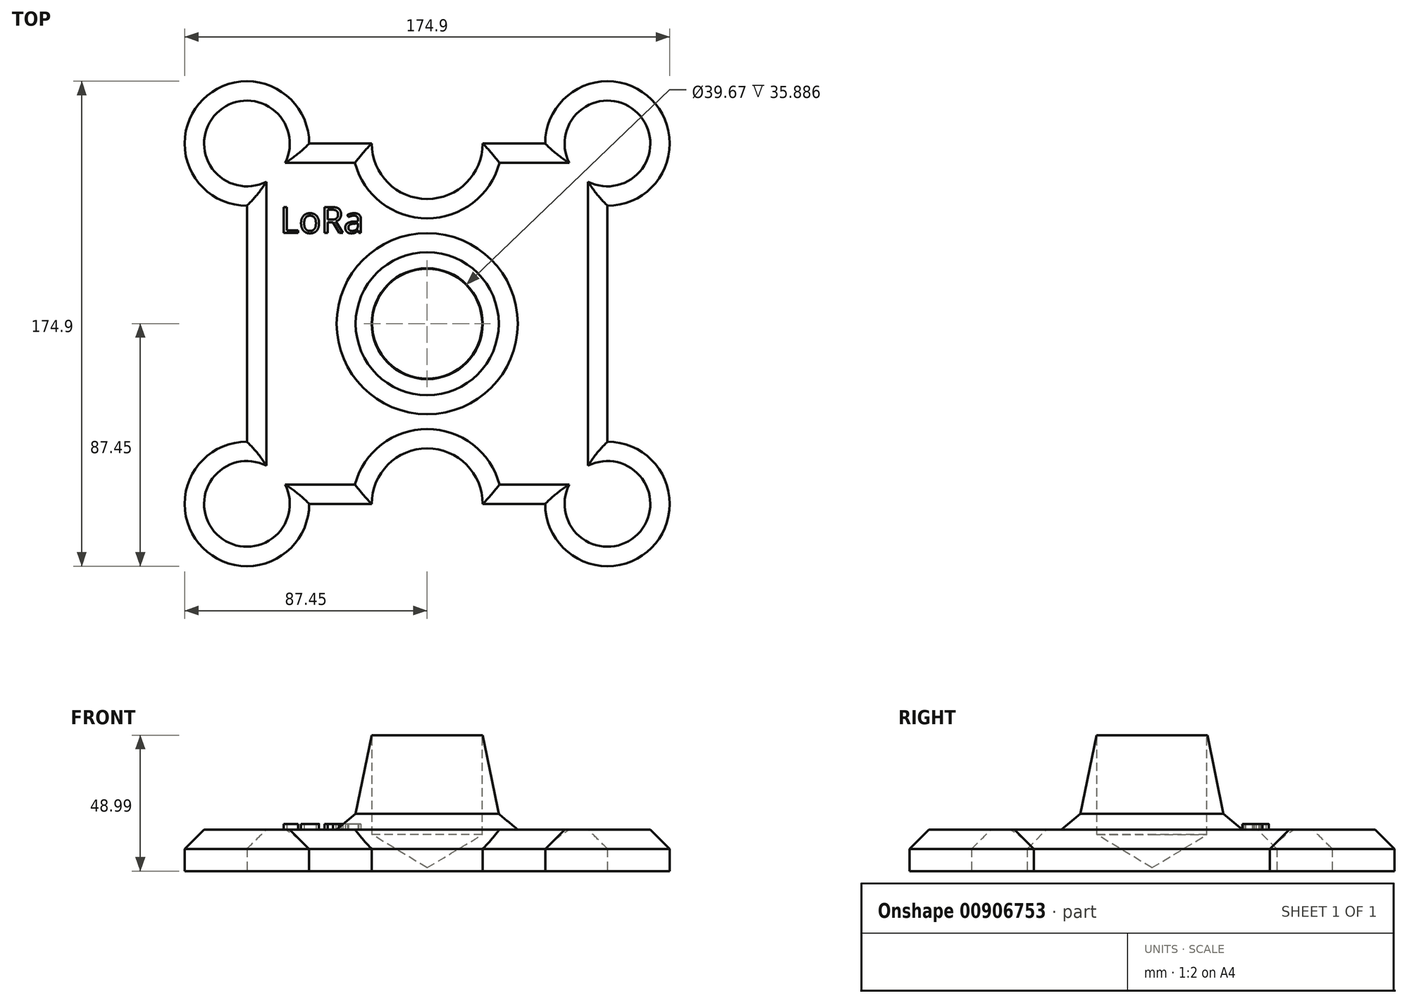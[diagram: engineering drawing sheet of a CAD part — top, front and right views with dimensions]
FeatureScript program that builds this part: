
annotation { "Feature Type Name" : "Feature", "Feature Type Description" : "" }
export const myFeature = defineFeature(function(context is Context, id is Id, definition is map)
    precondition{}
    {
        {
            var Q0;
            Q0=qCreatedBy(makeId("Top.planeOp"),FACE);
            var sketch = newSketch(context, id + "F0", { "sketchPlane" : qUnion([Q0])});
            skLineSegment(sketch, "E0.bottom", {"start": v(-42.55, 65) * mm, "end": v(-20, 65) * mm});
            skLineSegment(sketch, "E0.top", {"start": v(-42.55, -65) * mm, "end": v(-20, -65) * mm});
            skLineSegment(sketch, "E0.left", {"start": v(-65, 42.55) * mm, "end": v(-65, -42.55) * mm});
            skLineSegment(sketch, "E0.right", {"start": v(65, 42.55) * mm, "end": v(65, -42.55) * mm});
            skPoint(sketch, "E0.middle", {"position": v(0, 0) * mm});
            skArc(sketch, "E1", {"start": v(-42.55, 65) * mm, "mid": v(-80.87, 80.87) * mm, "end": v(-65, 42.55) * mm});
            skArc(sketch, "E2.1.0.0", {"start": v(-20, 65) * mm, "mid": v(0, 45) * mm, "end": v(20, 65) * mm});
            skArc(sketch, "E2.2.0.0", {"start": v(65, 42.55) * mm, "mid": v(80.87, 80.87) * mm, "end": v(42.55, 65) * mm});
            skLineSegment(sketch, "E2.direction1", {"start": v(-42.55, 65) * mm, "end": v(-20, 65) * mm, "construction": true});
            skArc(sketch, "E3.0.1.0", {"start": v(-65, -42.55) * mm, "mid": v(-80.87, -80.87) * mm, "end": v(-42.55, -65) * mm});
            skArc(sketch, "E3.1.1.0", {"start": v(20, -65) * mm, "mid": v(0, -45) * mm, "end": v(-20, -65) * mm});
            skArc(sketch, "E3.2.1.0", {"start": v(42.55, -65) * mm, "mid": v(80.87, -80.87) * mm, "end": v(65, -42.55) * mm});
            skLineSegment(sketch, "E3.direction2", {"start": v(-65, 42.55) * mm, "end": v(-65, -42.55) * mm, "construction": true});
            skLineSegment(sketch, "E4.trimOffspring", {"start": v(20, 65) * mm, "end": v(42.55, 65) * mm});
            skLineSegment(sketch, "E5.trimOffspring", {"start": v(20, -65) * mm, "end": v(42.55, -65) * mm});
            skSolve(sketch);
        }
        {
            var Q0;
            Q0=makeQuery(id+"F0.imprint","IMPRINT",FACE,{"disambiguationData":[TD([[makeQuery(id+"F0.imprint","IMPRINT",EDGE,{"derivedFrom":sQuery(id+"F0.wireOp",EDGE,"E0.bottom")}),-1.0]])]});
            extrude(context, id + "F1", {"entities" : qUnion([Q0]), "depth" : 15 * mm, "offsetDistance" : 25 * mm});
        }
        {
            var Q0;
            Q0=qCreatedBy(makeId("Front.planeOp"),FACE);
            var sketch = newSketch(context, id + "F2", { "sketchPlane" : qUnion([Q0])});
            skLineSegment(sketch, "E6", {"start": v(0, 0) * mm, "end": v(30, 0) * mm});
            skLineSegment(sketch, "E7", {"start": v(30, 0) * mm, "end": v(20, 48.99) * mm});
            skLineSegment(sketch, "E8", {"start": v(20, 48.99) * mm, "end": v(0, 48.99) * mm});
            skLineSegment(sketch, "E9", {"start": v(0, 48.99) * mm, "end": v(0, 0) * mm});
            skSolve(sketch);
        }
        {
            var Q0;
            Q0 = qSketchRegion(id + "F2", true);
            var Q1;
            Q1=sQuery(id+"F2.wireOp",EDGE,"E9");
            revolve(context, id + "F3", {"operationType" : NewBodyOperationType.ADD, "surfaceOperationType" : NewSurfaceOperationType.NEW, "entities" : qUnion([Q0]), "axis" : qUnion([Q1]), "revolveType" : RevolveType.FULL});
        }
        {
            var Q0;
            Q0=makeQuery(id+"F3.opRevolve","SWEPT_FACE",FACE,{"disambiguationData":[OSD([sQuery(id+"F2.wireOp",EDGE,"E8")])]});
            var sketch = newSketch(context, id + "F4", { "sketchPlane" : qUnion([Q0])});
            skCircle(sketch, "E10", {"center": v(0, 0) * mm, "radius": 29.1 * mm});
            skSolve(sketch);
        }
        {
            var Q0;
            Q0=sQuery(id+"F4.wireOp",VERTEX,"E10.center");
            var Q1;
            Q1=makeQuery(id+"F1.opExtrude","SWEPT_BODY",BODY,{"disambiguationData":[OSD([sQuery(id+"F0.wireOp",EDGE,"E0.bottom"),sQuery(id+"F0.wireOp",EDGE,"E0.top"),sQuery(id+"F0.wireOp",EDGE,"E0.left"),sQuery(id+"F0.wireOp",EDGE,"E0.right"),sQuery(id+"F0.wireOp",EDGE,"E1"),sQuery(id+"F0.wireOp",EDGE,"E2.1.0.0"),sQuery(id+"F0.wireOp",EDGE,"E2.2.0.0"),sQuery(id+"F0.wireOp",EDGE,"E3.0.1.0"),sQuery(id+"F0.wireOp",EDGE,"E3.1.1.0"),sQuery(id+"F0.wireOp",EDGE,"E3.2.1.0"),sQuery(id+"F0.wireOp",EDGE,"E4.trimOffspring"),sQuery(id+"F0.wireOp",EDGE,"E5.trimOffspring")])]});
            hole(context, id + "F5", {"style" : HoleStyle.SIMPLE, "endStyle" : HoleEndStyle.BLIND, "standardTappedOrClearance" : lookupTablePath({ "fit" : "Close (ASME)", "standard" : "ANSI", "size" : "1 1/2", "type" : "Clearance" }), "standardBlindInLast" : lookupTablePath({ "fit" : "Close", "standard" : "ANSI", "size" : "1 1/2", "type" : "Clearance" }), "holeDiameter" : 39.67 * mm, "majorDiameter" : 31.75 * mm, "holeDepth" : 35.9 * mm, "isTappedThrough" : true, "tappedDepth" : 12 * mm, "tapClearance" : 3, "locations" : qUnion([Q0]), "scope" : qUnion([Q1])});
        }
        {
            var Q0;
            Q0=makeQuery(id+"F1.opExtrude","CAP_FACE",FACE,{"disambiguationData":[OSD([sQuery(id+"F0.wireOp",EDGE,"E0.bottom"),sQuery(id+"F0.wireOp",EDGE,"E0.top"),sQuery(id+"F0.wireOp",EDGE,"E0.left"),sQuery(id+"F0.wireOp",EDGE,"E0.right"),sQuery(id+"F0.wireOp",EDGE,"E1"),sQuery(id+"F0.wireOp",EDGE,"E2.1.0.0"),sQuery(id+"F0.wireOp",EDGE,"E2.2.0.0"),sQuery(id+"F0.wireOp",EDGE,"E3.0.1.0"),sQuery(id+"F0.wireOp",EDGE,"E3.1.1.0"),sQuery(id+"F0.wireOp",EDGE,"E3.2.1.0"),sQuery(id+"F0.wireOp",EDGE,"E4.trimOffspring"),sQuery(id+"F0.wireOp",EDGE,"E5.trimOffspring")])],"isStart":false});
            chamfer(context, id + "F6", {"entities" : qUnion([Q0]), "width" : 7 * mm, "tangentPropagation" : true});
        }
        {
            var Q0;
            Q0=makeQuery(id+"F1.opExtrude","CAP_FACE",FACE,{"disambiguationData":[OSD([sQuery(id+"F0.wireOp",EDGE,"E0.bottom"),sQuery(id+"F0.wireOp",EDGE,"E0.top"),sQuery(id+"F0.wireOp",EDGE,"E0.left"),sQuery(id+"F0.wireOp",EDGE,"E0.right"),sQuery(id+"F0.wireOp",EDGE,"E1"),sQuery(id+"F0.wireOp",EDGE,"E2.1.0.0"),sQuery(id+"F0.wireOp",EDGE,"E2.2.0.0"),sQuery(id+"F0.wireOp",EDGE,"E3.0.1.0"),sQuery(id+"F0.wireOp",EDGE,"E3.1.1.0"),sQuery(id+"F0.wireOp",EDGE,"E3.2.1.0"),sQuery(id+"F0.wireOp",EDGE,"E4.trimOffspring"),sQuery(id+"F0.wireOp",EDGE,"E5.trimOffspring")])],"isStart":false});
            var sketch = newSketch(context, id + "F7", { "sketchPlane" : qUnion([Q0])});
            skText(sketch, "E11", { "text": "LoRa", "fontName": "OpenSans-Regular.ttf"});
            const initialGuessF7  = {"E11": [-0.05304, 0.0327, 1, 0, 0.00947]};
            skSetInitialGuess(sketch, initialGuessF7);
            skSolve(sketch);
        }
        {
            var Q0;
            Q0 = qSketchRegion(id + "F7", true);
            extrude(context, id + "F8", {"entities" : qUnion([Q0]), "operationType" : NewBodyOperationType.ADD, "depth" : 2 * mm, "offsetDistance" : 25 * mm});
        }
    });
